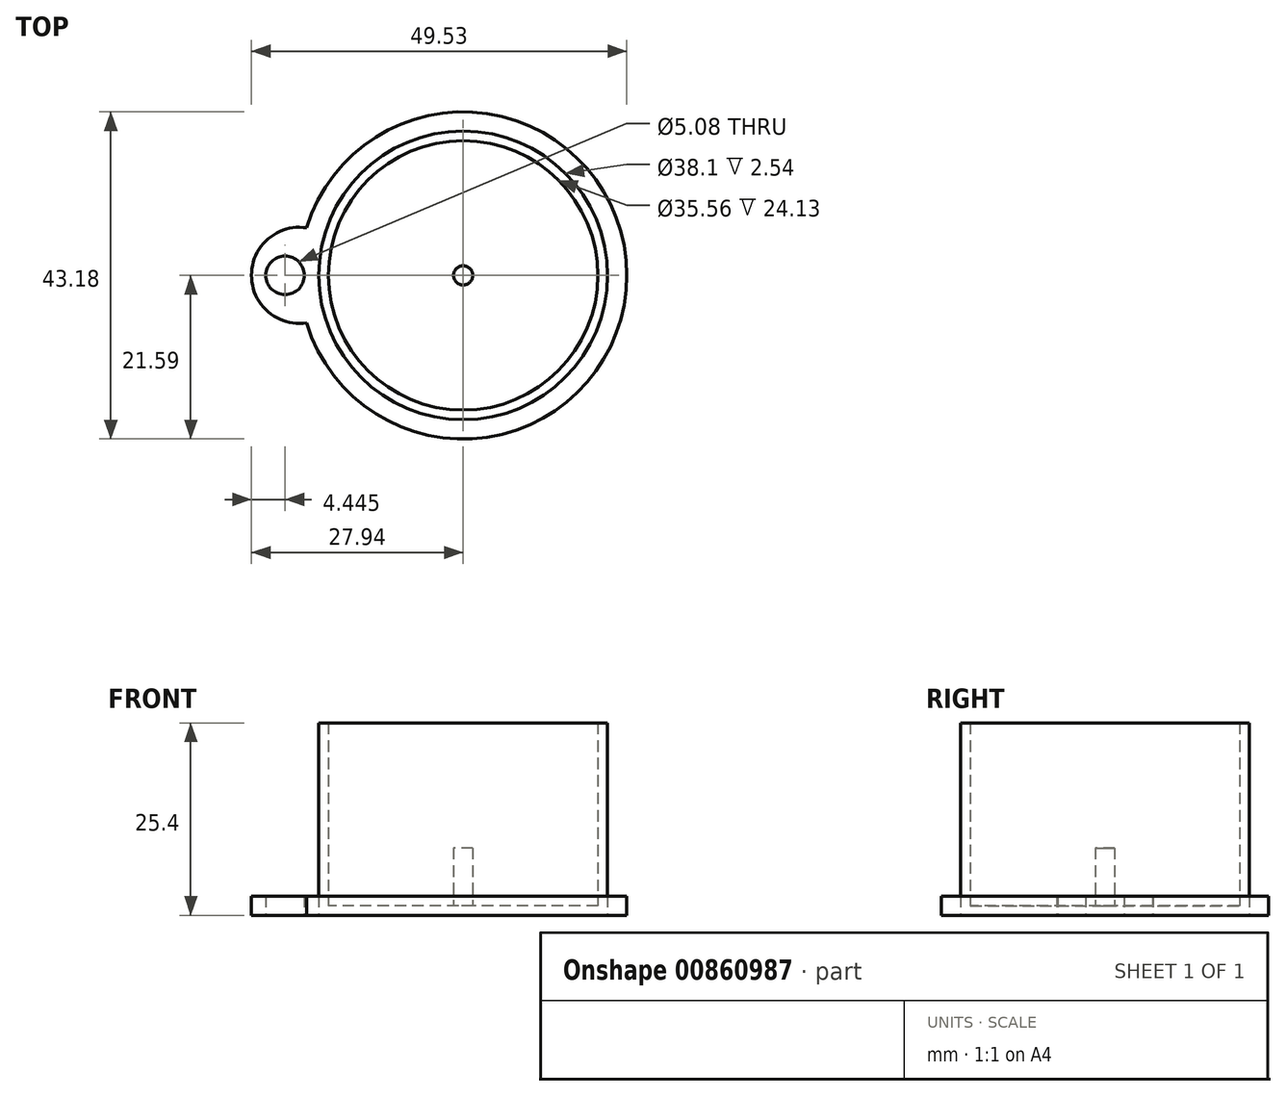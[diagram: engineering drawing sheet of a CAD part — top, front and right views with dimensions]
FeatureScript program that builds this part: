
annotation { "Feature Type Name" : "Feature", "Feature Type Description" : "" }
export const myFeature = defineFeature(function(context is Context, id is Id, definition is map)
    precondition{}
    {
        {
            var Q0;
            Q0=qCreatedBy(makeId("Top.planeOp"),FACE);
            var sketch = newSketch(context, id + "F0", { "sketchPlane" : qUnion([Q0])});
            skCircle(sketch, "E0", {"center": v(0, 0) * mm, "radius": 19.05 * mm});
            skSolve(sketch);
        }
        {
            var Q0;
            Q0=makeQuery(id+"F0.imprint","IMPRINT",FACE,{"disambiguationData":[TD([[makeQuery(id+"F0.imprint","IMPRINT",EDGE,{"derivedFrom":sQuery(id+"F0.wireOp",EDGE,"E0")}),1.0]])]});
            extrude(context, id + "F1", {"entities" : qUnion([Q0]), "depth" : 25.4 * mm, "offsetDistance" : 25.4 * mm});
        }
        {
            var Q0;
            Q0=makeQuery(id+"F1.opExtrude","CAP_FACE",FACE,{"disambiguationData":[OSD([sQuery(id+"F0.wireOp",EDGE,"E0")])],"isStart":false});
            shell(context, id + "F2", {"entities" : qUnion([Q0]), "thickness" : 1.27 * mm});
        }
        {
            var Q0;
            Q0=makeQuery(id+"F1.opExtrude","CAP_FACE",FACE,{"disambiguationData":[OSD([sQuery(id+"F0.wireOp",EDGE,"E0")])],"isStart":true});
            var sketch = newSketch(context, id + "F3", { "sketchPlane" : qUnion([Q0])});
            skArc(sketch, "E1", {"start": v(-20.66, -6.28) * mm, "mid": v(21.59, 0) * mm, "end": v(-20.66, 6.28) * mm});
            skArc(sketch, "E2", {"start": v(-20.66, 6.28) * mm, "mid": v(-27.94, 0) * mm, "end": v(-20.66, -6.28) * mm});
            skCircle(sketch, "E3", {"center": v(-23.5, 0) * mm, "radius": 2.54 * mm});
            skCircle(sketch, "E4.0", {"center": v(0, 0) * mm, "radius": 19.05 * mm});
            skSolve(sketch);
        }
        {
            var Q0;
            Q0=makeQuery(id+"F3.imprint","IMPRINT",FACE,{"disambiguationData":[TD([[makeQuery(id+"F3.imprint","IMPRINT",EDGE,{"derivedFrom":sQuery(id+"F3.wireOp",EDGE,"E1")}),1.0]])]});
            extrude(context, id + "F4", {"entities" : qUnion([Q0]), "oppositeDirection" : true, "depth" : 2.54 * mm, "offsetDistance" : 25.4 * mm});
        }
        {
            var Q0;
            {var subQ0=sQuery(id+"F0.wireOp",EDGE,"E0");Q0=makeQuery(id+"F2.opShell","OFFSET_FACE",FACE,{"disambiguationData":[OSD([subQ0]),TDD([makeQuery(id+"F1.opExtrude","CAP_FACE",FACE,{"disambiguationData":[OSD([subQ0])],"isStart":true})])]});}
            var sketch = newSketch(context, id + "F5", { "sketchPlane" : qUnion([Q0])});
            skCircle(sketch, "E5", {"center": v(0, 0) * mm, "radius": 1.27 * mm});
            skSolve(sketch);
        }
        {
            var Q0;
            Q0=makeQuery(id+"F5.imprint","IMPRINT",FACE,{"disambiguationData":[TD([[makeQuery(id+"F5.imprint","IMPRINT",EDGE,{"derivedFrom":sQuery(id+"F5.wireOp",EDGE,"E5")}),1.0]])]});
            extrude(context, id + "F6", {"entities" : qUnion([Q0]), "operationType" : NewBodyOperationType.ADD, "depth" : 7.62 * mm, "offsetDistance" : 25.4 * mm});
        }
    });
